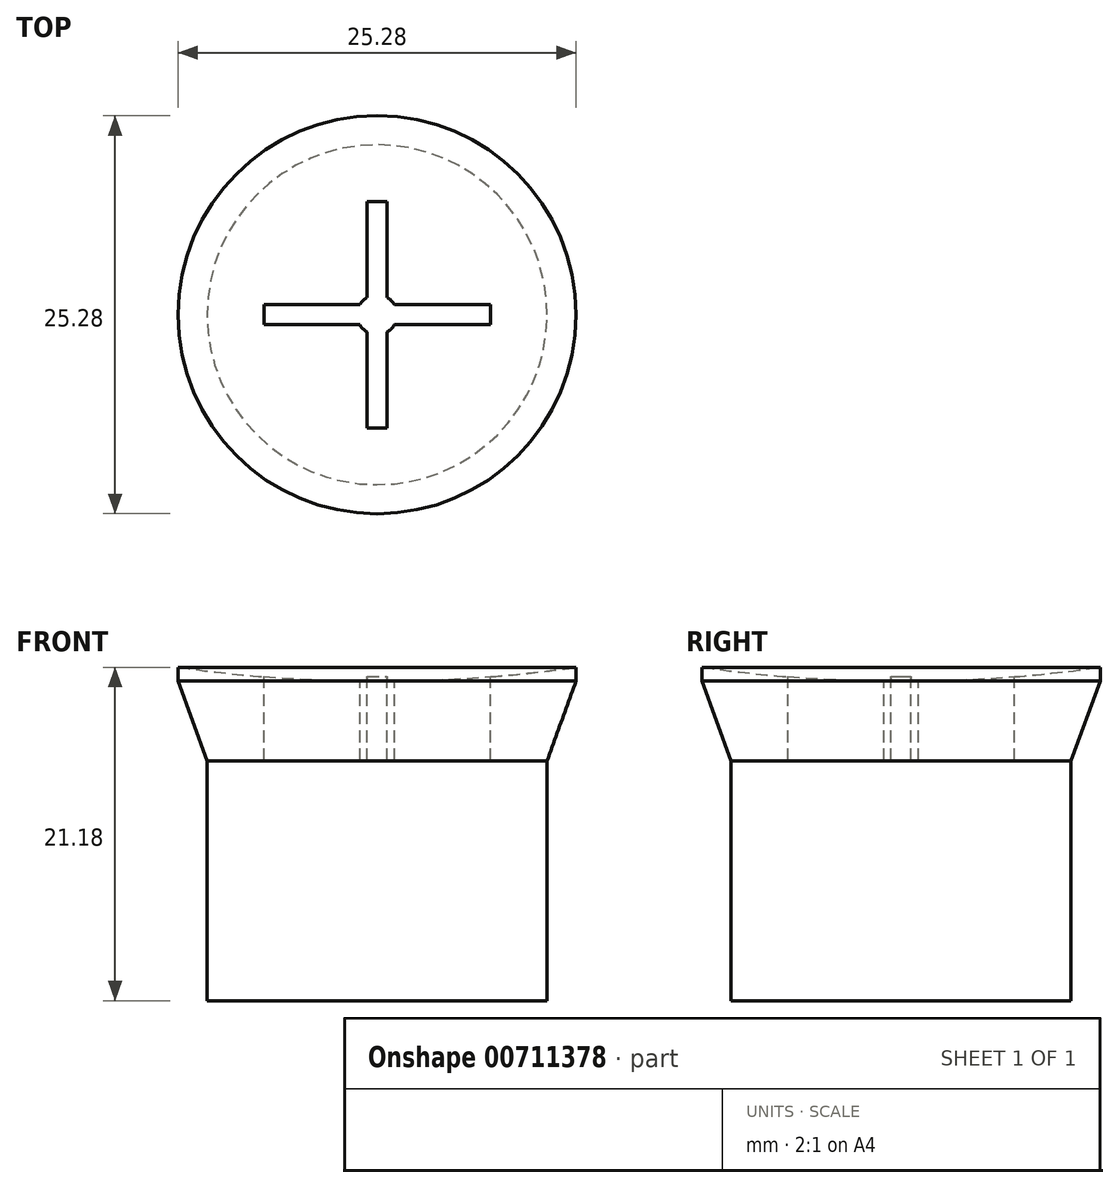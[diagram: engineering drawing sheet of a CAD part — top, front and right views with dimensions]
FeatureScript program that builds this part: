
annotation { "Feature Type Name" : "Feature", "Feature Type Description" : "" }
export const myFeature = defineFeature(function(context is Context, id is Id, definition is map)
    precondition{}
    {
        {
            var Q0;
            Q0=qCreatedBy(makeId("Top.planeOp"),FACE);
            var sketch = newSketch(context, id + "F0", { "sketchPlane" : qUnion([Q0])});
            skCircle(sketch, "E0", {"center": v(0, 0) * mm, "radius": 10.8 * mm});
            skSolve(sketch);
        }
        {
            var Q0;
            Q0 = qSketchRegion(id + "F0", true);
            extrude(context, id + "F1", {"entities" : qUnion([Q0]), "depth" : 15.24 * mm, "offsetDistance" : 25.4 * mm});
        }
        {
            var Q0;
            Q0=makeQuery(id+"F1.opExtrude","CAP_FACE",FACE,{"disambiguationData":[OSD([sQuery(id+"F0.wireOp",EDGE,"E0")])],"isStart":false});
            extrude(context, id + "F2", {"entities" : qUnion([Q0]), "operationType" : NewBodyOperationType.ADD, "depth" : 5.08 * mm, "offsetDistance" : 25.4 * mm, "hasDraft" : true, "draftAngle" : 20 * degree});
        }
        {
            var Q0;
            Q0=makeQuery(id+"F2.opExtrude","CAP_FACE",FACE,{"disambiguationData":[OSD([sQuery(id+"F0.wireOp",EDGE,"E0")])],"isStart":false});
            extrude(context, id + "F3", {"entities" : qUnion([Q0]), "operationType" : NewBodyOperationType.ADD, "depth" : 1.02 * mm, "offsetDistance" : 25.4 * mm});
        }
        {
            var Q0;
            Q0=makeQuery(id+"F3.opExtrude","CAP_FACE",FACE,{"disambiguationData":[OSD([sQuery(id+"F0.wireOp",EDGE,"E0")])],"isStart":false});
            var sketch = newSketch(context, id + "F4", { "sketchPlane" : qUnion([Q0])});
            skLineSegment(sketch, "E1", {"start": v(0, 12.64) * mm, "end": v(0, -12.64) * mm, "construction": true});
            skLineSegment(sketch, "E2", {"start": v(-12.64, 0) * mm, "end": v(12.64, 0) * mm, "construction": true});
            skLineSegment(sketch, "E3.bottom", {"start": v(-0.63, 7.2) * mm, "end": v(0.64, 7.2) * mm});
            skLineSegment(sketch, "E3.left", {"start": v(-0.63, 7.2) * mm, "end": v(-0.64, 1.1) * mm});
            skLineSegment(sketch, "E3.right", {"start": v(0.64, 7.2) * mm, "end": v(0.64, 1.1) * mm});
            skLineSegment(sketch, "E4.bottom", {"start": v(-7.2, 0.64) * mm, "end": v(-1.1, 0.64) * mm});
            skLineSegment(sketch, "E4.top", {"start": v(-7.2, -0.64) * mm, "end": v(-1.1, -0.64) * mm});
            skLineSegment(sketch, "E4.left", {"start": v(-7.2, 0.64) * mm, "end": v(-7.2, -0.64) * mm});
            skLineSegment(sketch, "E5.top", {"start": v(-0.64, -7.2) * mm, "end": v(0.63, -7.2) * mm});
            skLineSegment(sketch, "E5.left", {"start": v(-0.64, -1.1) * mm, "end": v(-0.64, -7.2) * mm});
            skLineSegment(sketch, "E5.right", {"start": v(0.63, -1.1) * mm, "end": v(0.63, -7.2) * mm});
            skLineSegment(sketch, "E6.bottom", {"start": v(1.1, 0.64) * mm, "end": v(7.2, 0.64) * mm});
            skLineSegment(sketch, "E6.top", {"start": v(1.1, -0.64) * mm, "end": v(7.2, -0.64) * mm});
            skLineSegment(sketch, "E6.right", {"start": v(7.2, 0.64) * mm, "end": v(7.2, -0.64) * mm});
            skCircle(sketch, "E7", {"center": v(0, 0) * mm, "radius": 1.27 * mm, "construction": true});
            skArc(sketch, "E8", {"start": v(-1.1, 0.64) * mm, "mid": v(-0.9, 0.9) * mm, "end": v(-0.63, 1.1) * mm});
            skArc(sketch, "E9", {"start": v(0.64, 1.1) * mm, "mid": v(0.9, 0.9) * mm, "end": v(1.1, 0.64) * mm});
            skArc(sketch, "E10", {"start": v(1.1, -0.63) * mm, "mid": v(0.9, -0.9) * mm, "end": v(0.63, -1.1) * mm});
            skArc(sketch, "E11", {"start": v(-0.64, -1.1) * mm, "mid": v(-0.9, -0.9) * mm, "end": v(-1.1, -0.63) * mm});
            skSolve(sketch);
        }
        {
            var Q0;
            Q0 = qSketchRegion(id + "F4", true);
            extrude(context, id + "F5", {"entities" : qUnion([Q0]), "operationType" : NewBodyOperationType.REMOVE, "oppositeDirection" : true, "depth" : 6.07 * mm, "offsetDistance" : 25.4 * mm});
        }
        {
            var Q0;
            Q0=qCreatedBy(makeId("Front.planeOp"),FACE);
            var sketch = newSketch(context, id + "F6", { "sketchPlane" : qUnion([Q0])});
            skLineSegment(sketch, "E12", {"start": v(0, 20.3) * mm, "end": v(0, 201.92) * mm});
            skArc(sketch, "E13", {"start": v(0, 201.92) * mm, "mid": v(-90.81, 111.1) * mm, "end": v(0, 20.3) * mm});
            skSolve(sketch);
        }
        {
            var Q0;
            Q0 = qSketchRegion(id + "F6", true);
            var Q1;
            Q1=sQuery(id+"F6.wireOp",EDGE,"E12");
            revolve(context, id + "F7", {"operationType" : NewBodyOperationType.REMOVE, "surfaceOperationType" : NewSurfaceOperationType.NEW, "entities" : qUnion([Q0]), "axis" : qUnion([Q1]), "revolveType" : RevolveType.FULL, "oppositeDirection" : true});
        }
    });
